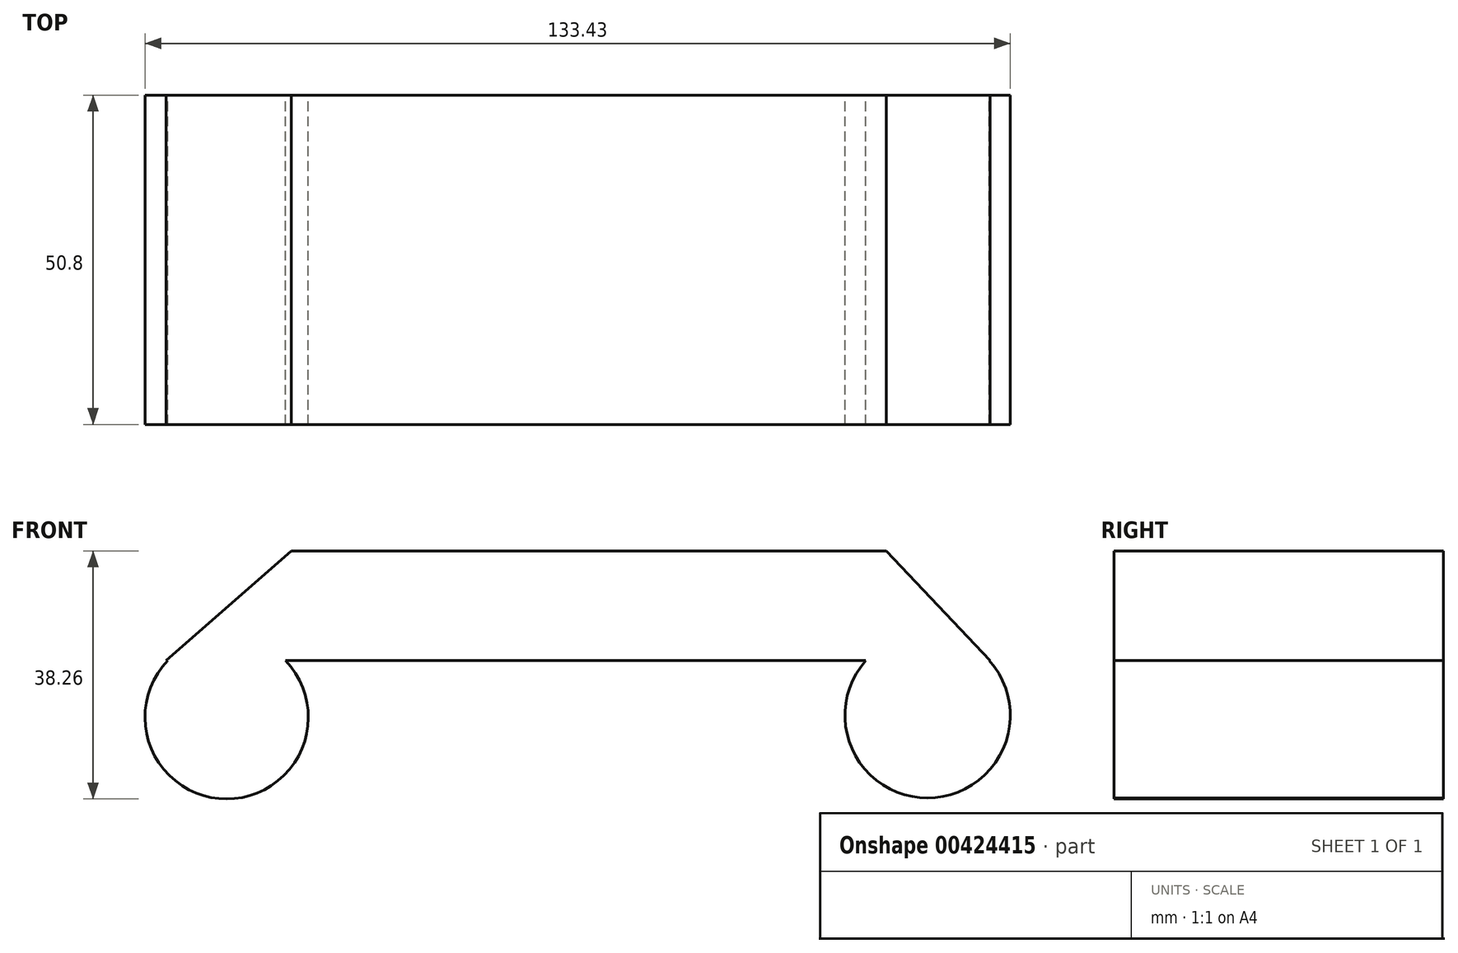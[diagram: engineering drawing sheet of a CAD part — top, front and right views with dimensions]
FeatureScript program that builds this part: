
annotation { "Feature Type Name" : "Feature", "Feature Type Description" : "" }
export const myFeature = defineFeature(function(context is Context, id is Id, definition is map)
    precondition{}
    {
        {
            var Q0;
            Q0=qCreatedBy(makeId("Front.planeOp"),FACE);
            var sketch = newSketch(context, id + "F0", { "sketchPlane" : qUnion([Q0])});
            skLineSegment(sketch, "E0", {"start": v(-67.93, 0) * mm, "end": v(-48.6, 16.9) * mm});
            skLineSegment(sketch, "E1", {"start": v(-48.6, 16.9) * mm, "end": v(43.18, 16.9) * mm});
            skLineSegment(sketch, "E2", {"start": v(43.18, 16.9) * mm, "end": v(59.18, 0) * mm});
            skLineSegment(sketch, "E3", {"start": v(59.18, 0) * mm, "end": v(-67.93, 0) * mm});
            skSolve(sketch);
        }
        {
            var Q0;
            Q0=makeQuery(id+"F0.imprint","IMPRINT",FACE,{"disambiguationData":[TD([[makeQuery(id+"F0.imprint","IMPRINT",EDGE,{"derivedFrom":sQuery(id+"F0.wireOp",EDGE,"E0")}),-1.0]])]});
            extrude(context, id + "F1", {"entities" : qUnion([Q0]), "depth" : 25.4 * mm});
        }
        {
            var Q0;
            Q0=makeQuery(id+"F1.opExtrude","CAP_FACE",FACE,{"disambiguationData":[OSD([sQuery(id+"F0.wireOp",EDGE,"E0"),sQuery(id+"F0.wireOp",EDGE,"E1"),sQuery(id+"F0.wireOp",EDGE,"E2"),sQuery(id+"F0.wireOp",EDGE,"E3")])],"isStart":true});
            extrude(context, id + "F2", {"entities" : qUnion([Q0]), "operationType" : NewBodyOperationType.ADD, "depth" : 25.4 * mm});
        }
        {
            var Q0;
            Q0=qCreatedBy(makeId("Front.planeOp"),FACE);
            var sketch = newSketch(context, id + "F3", { "sketchPlane" : qUnion([Q0])});
            skCircle(sketch, "E4", {"center": v(-58.57, -8.76) * mm, "radius": 12.6 * mm});
            skCircle(sketch, "E5", {"center": v(49.52, -8.45) * mm, "radius": 12.74 * mm});
            skSolve(sketch);
        }
        {
            var Q0;
            Q0=makeQuery(id+"F3.imprint","IMPRINT",FACE,{"disambiguationData":[TD([[makeQuery(id+"F3.imprint","IMPRINT",EDGE,{"derivedFrom":sQuery(id+"F3.wireOp",EDGE,"E5")}),1.0]])]});
            extrude(context, id + "F4", {"entities" : qUnion([Q0]), "operationType" : NewBodyOperationType.ADD, "depth" : 25.4 * mm});
        }
        {
            var Q0;
            Q0=makeQuery(id+"F4.opExtrude","CAP_FACE",FACE,{"disambiguationData":[OSD([sQuery(id+"F3.wireOp",EDGE,"E5")])],"isStart":true});
            extrude(context, id + "F5", {"entities" : qUnion([Q0]), "operationType" : NewBodyOperationType.ADD, "depth" : 25.4 * mm});
        }
        {
            var Q0;
            Q0 = qSketchRegion(id + "F3", true);
            extrude(context, id + "F6", {"entities" : qUnion([Q0]), "operationType" : NewBodyOperationType.ADD, "depth" : 25.4 * mm});
        }
        {
            var Q0;
            Q0=makeQuery(id+"F6.opExtrude","CAP_FACE",FACE,{"disambiguationData":[OSD([sQuery(id+"F3.wireOp",EDGE,"E4")])],"isStart":true});
            extrude(context, id + "F7", {"entities" : qUnion([Q0]), "operationType" : NewBodyOperationType.ADD, "depth" : 25.4 * mm});
        }
    });
